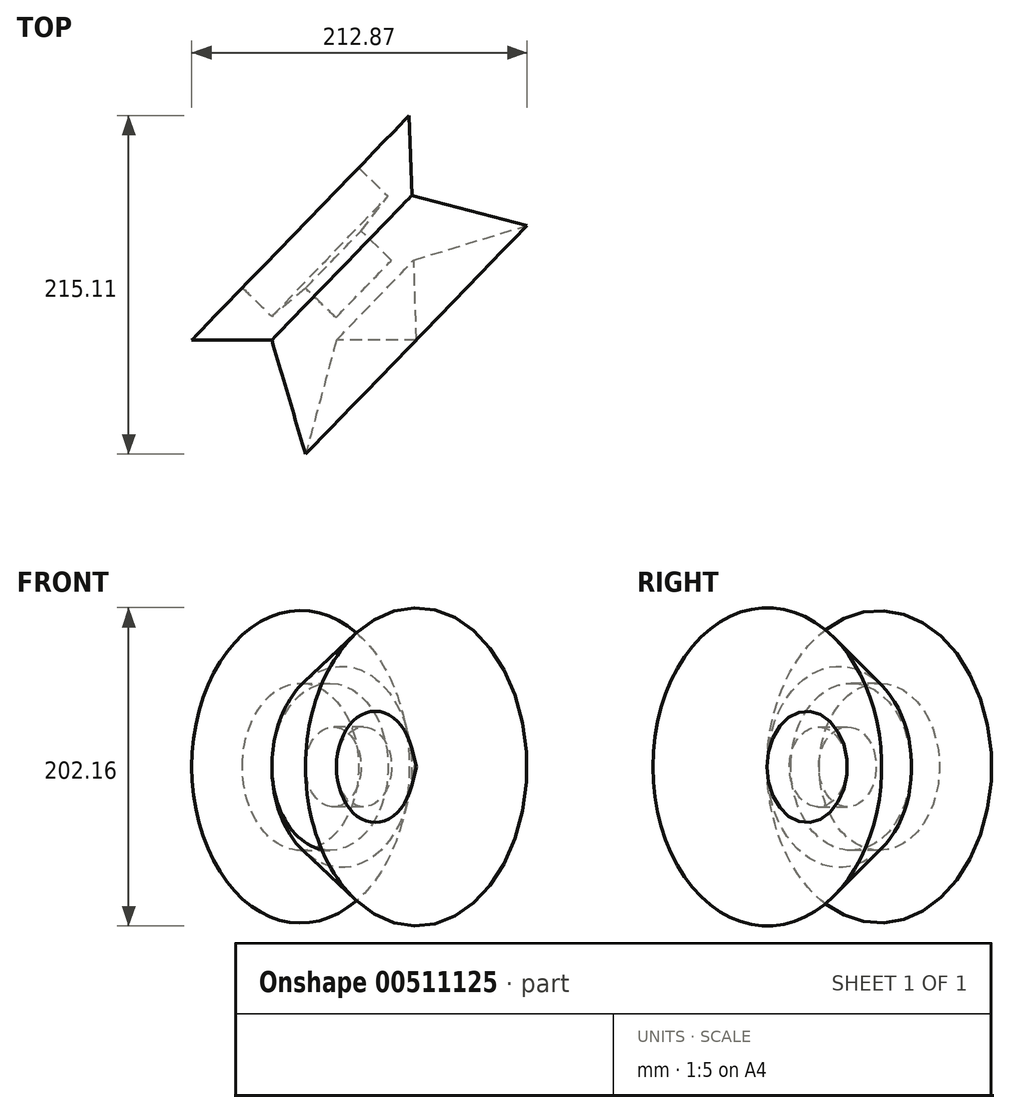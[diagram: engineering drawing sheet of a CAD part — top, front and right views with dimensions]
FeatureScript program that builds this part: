
annotation { "Feature Type Name" : "Feature", "Feature Type Description" : "" }
export const myFeature = defineFeature(function(context is Context, id is Id, definition is map)
    precondition{}
    {
        {
            var Q0;
            Q0=qCreatedBy(makeId("Top.planeOp"),FACE);
            var sketch = newSketch(context, id + "F0", { "sketchPlane" : qUnion([Q0])});
            skLineSegment(sketch, "E0", {"start": v(0, 46.73) * mm, "end": v(19.3, 28.04) * mm});
            skLineSegment(sketch, "E1", {"start": v(19.3, 28.04) * mm, "end": v(36.94, 46.25) * mm});
            skLineSegment(sketch, "E2", {"start": v(36.94, 46.25) * mm, "end": v(70.4, 13.85) * mm});
            skLineSegment(sketch, "E3", {"start": v(70.4, 13.85) * mm, "end": v(19.6, 13.85) * mm});
            skLineSegment(sketch, "E4", {"start": v(19.6, 13.85) * mm, "end": v(0, -58.68) * mm});
            skLineSegment(sketch, "E5", {"start": v(0, -58.68) * mm, "end": v(-21.45, 13.85) * mm});
            skLineSegment(sketch, "E6", {"start": v(-21.45, 13.85) * mm, "end": v(-72.25, 13.85) * mm});
            skLineSegment(sketch, "E7", {"start": v(-72.25, 13.85) * mm, "end": v(-40.15, 47) * mm});
            skLineSegment(sketch, "E8", {"start": v(-40.15, 47) * mm, "end": v(-21.45, 28.9) * mm});
            skLineSegment(sketch, "E9", {"start": v(-21.45, 28.9) * mm, "end": v(0, 46.73) * mm});
            skSolve(sketch);
        }
        {
            var Q0;
            Q0=makeQuery(id+"F0.imprint","IMPRINT",FACE,{"disambiguationData":[TD([[makeQuery(id+"F0.imprint","IMPRINT",EDGE,{"derivedFrom":sQuery(id+"F0.wireOp",EDGE,"E0")}),-1.0]])]});
            var Q1;
            Q1=sQuery(id+"F0.wireOp",EDGE,"E2");
            revolve(context, id + "F1", {"entities" : qUnion([Q0]), "axis" : qUnion([Q1]), "revolveType" : RevolveType.FULL});
        }
    });
